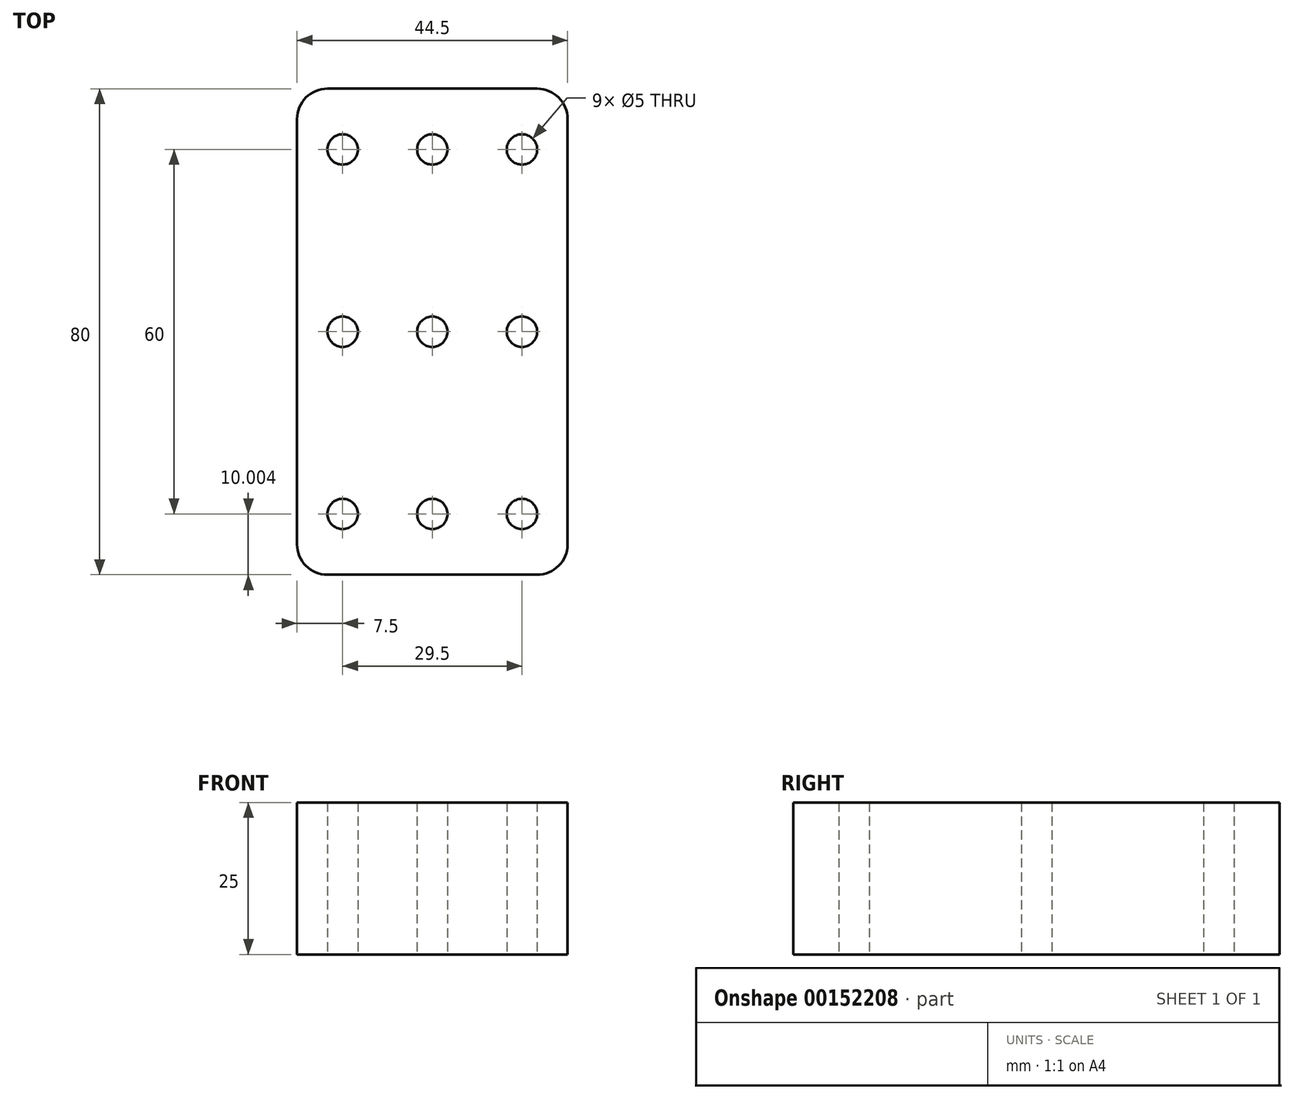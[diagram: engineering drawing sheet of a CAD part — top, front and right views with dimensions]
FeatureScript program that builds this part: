
annotation { "Feature Type Name" : "Feature", "Feature Type Description" : "" }
export const myFeature = defineFeature(function(context is Context, id is Id, definition is map)
    precondition{}
    {
        {
            var Q0;
            Q0=qCreatedBy(makeId("Top.planeOp"),FACE);
            var sketch = newSketch(context, id + "F0", { "sketchPlane" : qUnion([Q0])});
            skLineSegment(sketch, "E0.bottom", {"start": v(-32.78, 29.34) * mm, "end": v(11.72, 29.34) * mm});
            skLineSegment(sketch, "E0.top", {"start": v(-32.78, -50.66) * mm, "end": v(11.72, -50.66) * mm});
            skLineSegment(sketch, "E0.left", {"start": v(-32.78, 29.34) * mm, "end": v(-32.78, -50.66) * mm});
            skLineSegment(sketch, "E0.right", {"start": v(11.72, 29.34) * mm, "end": v(11.72, -50.66) * mm});
            skLineSegment(sketch, "E1", {"start": v(-25.28, 29.34) * mm, "end": v(-25.28, -50.66) * mm, "construction": true});
            skLineSegment(sketch, "E2", {"start": v(-25.28, -50.66) * mm, "end": v(4.22, -50.66) * mm, "construction": true});
            skLineSegment(sketch, "E3", {"start": v(4.22, -50.66) * mm, "end": v(4.22, 29.34) * mm, "construction": true});
            skLineSegment(sketch, "E4", {"start": v(11.72, 19.34) * mm, "end": v(-32.78, 19.34) * mm, "construction": true});
            skLineSegment(sketch, "E5", {"start": v(-32.78, 19.34) * mm, "end": v(-32.78, -10.66) * mm, "construction": true});
            skLineSegment(sketch, "E6", {"start": v(-32.78, -10.66) * mm, "end": v(11.72, -10.66) * mm, "construction": true});
            skLineSegment(sketch, "E7", {"start": v(11.72, -10.66) * mm, "end": v(11.72, -40.66) * mm, "construction": true});
            skLineSegment(sketch, "E8", {"start": v(11.72, -40.66) * mm, "end": v(-32.78, -40.66) * mm, "construction": true});
            skLineSegment(sketch, "E9", {"start": v(-10.53, 29.34) * mm, "end": v(-10.53, -50.66) * mm, "construction": true});
            skLineSegment(sketch, "E10", {"start": v(4.22, 29.34) * mm, "end": v(11.72, 29.34) * mm});
            skLineSegment(sketch, "E11", {"start": v(-32.78, 29.34) * mm, "end": v(-32.78, 19.34) * mm});
            skCircle(sketch, "E12", {"center": v(-25.28, 19.34) * mm, "radius": 2.5 * mm});
            skCircle(sketch, "E13", {"center": v(-10.53, 19.34) * mm, "radius": 2.5 * mm});
            skCircle(sketch, "E14", {"center": v(4.22, 19.34) * mm, "radius": 2.5 * mm});
            skCircle(sketch, "E15", {"center": v(-25.28, -10.66) * mm, "radius": 2.5 * mm});
            skCircle(sketch, "E16", {"center": v(-10.53, -10.66) * mm, "radius": 2.5 * mm});
            skCircle(sketch, "E17", {"center": v(4.22, -10.66) * mm, "radius": 2.5 * mm});
            skCircle(sketch, "E18", {"center": v(-25.28, -40.66) * mm, "radius": 2.5 * mm});
            skCircle(sketch, "E19", {"center": v(-10.53, -40.66) * mm, "radius": 2.5 * mm});
            skCircle(sketch, "E20", {"center": v(4.22, -40.66) * mm, "radius": 2.5 * mm});
            skSolve(sketch);
        }
        {
            var Q0;
            Q0=makeQuery(id+"F0.imprint","IMPRINT",FACE,{"disambiguationData":[TD([[makeQuery(id+"F0.imprint","IMPRINT",EDGE,{"derivedFrom":sQuery(id+"F0.wireOp",EDGE,"E0.bottom")}),-1.0]])]});
            extrude(context, id + "F1", {"entities" : qUnion([Q0]), "depth" : 25 * mm});
        }
        {
            var Q0;
            Q0=makeQuery(id+"F1.opExtrude","SWEPT_EDGE",EDGE,{"disambiguationData":[OSD([sQuery(id+"F0.wireOp",EDGE,"E0.top"),sQuery(id+"F0.wireOp",EDGE,"E0.left")])]});
            var Q1;
            Q1=makeQuery(id+"F1.opExtrude","SWEPT_EDGE",EDGE,{"disambiguationData":[OSD([sQuery(id+"F0.wireOp",EDGE,"E0.top"),sQuery(id+"F0.wireOp",EDGE,"E0.right")])]});
            var Q2;
            Q2=makeQuery(id+"F1.opExtrude","SWEPT_EDGE",EDGE,{"disambiguationData":[OSD([sQuery(id+"F0.wireOp",EDGE,"E0.bottom"),sQuery(id+"F0.wireOp",EDGE,"E11")])]});
            var Q3;
            Q3=makeQuery(id+"F1.opExtrude","SWEPT_EDGE",EDGE,{"disambiguationData":[OSD([sQuery(id+"F0.wireOp",EDGE,"E0.right"),sQuery(id+"F0.wireOp",EDGE,"E10")])]});
            fillet(context, id + "F2", {"entities" : qUnion([Q0, Q1, Q2, Q3]), "radius" : 5 * mm, "tangentPropagation" : true, "allowEdgeOverflow" : false});
        }
    });
